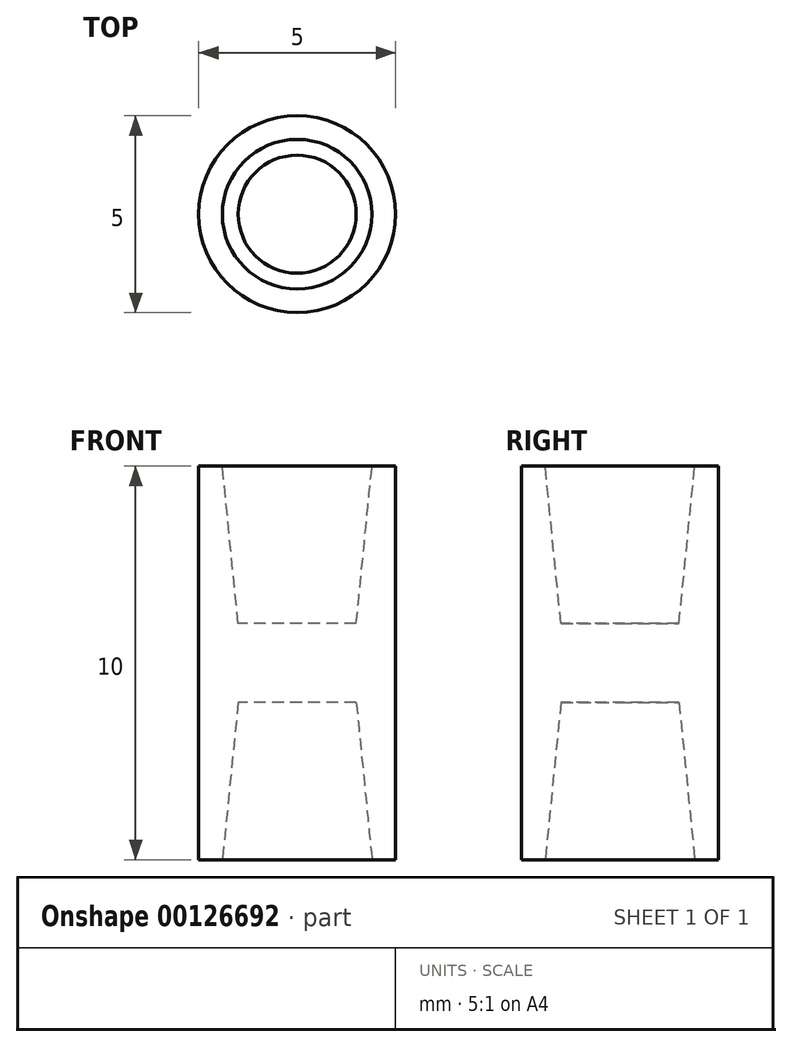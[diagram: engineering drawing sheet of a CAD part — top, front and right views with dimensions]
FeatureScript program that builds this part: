
annotation { "Feature Type Name" : "Feature", "Feature Type Description" : "" }
export const myFeature = defineFeature(function(context is Context, id is Id, definition is map)
    precondition{}
    {
        {
            var Q0;
            Q0=qCreatedBy(makeId("Top.planeOp"),FACE);
            var sketch = newSketch(context, id + "F0", { "sketchPlane" : qUnion([Q0])});
            skCircle(sketch, "E0", {"center": v(0, 0) * mm, "radius": 1.5 * mm});
            skCircle(sketch, "E1", {"center": v(0, 0) * mm, "radius": 2.5 * mm});
            skPoint(sketch, "E2", {"position": v(1.5, 0) * mm});
            skPoint(sketch, "E3", {"position": v(2.5, 0) * mm});
            skSolve(sketch);
        }
        {
            var Q0;
            Q0=makeQuery(id+"F0.imprint","IMPRINT",FACE,{"disambiguationData":[TD([[makeQuery(id+"F0.imprint","IMPRINT",EDGE,{"derivedFrom":sQuery(id+"F0.wireOp",EDGE,"E0")}),1.0]])]});
            extrude(context, id + "F1", {"entities" : qUnion([Q0]), "endBound" : BoundingType.SYMMETRIC, "depth" : 2 * mm});
        }
        {
            var Q0;
            Q0=makeQuery(id+"F0.imprint","IMPRINT",FACE,{"disambiguationData":[TD([[makeQuery(id+"F0.imprint","IMPRINT",EDGE,{"derivedFrom":sQuery(id+"F0.wireOp",EDGE,"E0")}),-1.0]])]});
            extrude(context, id + "F2", {"entities" : qUnion([Q0]), "operationType" : NewBodyOperationType.ADD, "endBound" : BoundingType.SYMMETRIC, "depth" : 10 * mm});
        }
        {
            var Q0;
            Q0=makeQuery(id+"F2.opExtrude","CAP_EDGE",EDGE,{"disambiguationData":[OSD([sQuery(id+"F0.wireOp",EDGE,"E0")])],"isStart":false});
            chamfer(context, id + "F3", {"entities" : qUnion([Q0]), "chamferType" : ChamferType.TWO_OFFSETS, "width1" : 4 * mm, "oppositeDirection" : false, "width2" : .4 * mm, "tangentPropagation" : true});
        }
        {
            var Q0;
            Q0=makeQuery(id+"F2.opExtrude","CAP_EDGE",EDGE,{"disambiguationData":[OSD([sQuery(id+"F0.wireOp",EDGE,"E0")])],"isStart":true});
            chamfer(context, id + "F4", {"entities" : qUnion([Q0]), "chamferType" : ChamferType.TWO_OFFSETS, "width1" : 0.4 * mm, "oppositeDirection" : false, "width2" : 4 * mm, "tangentPropagation" : true});
        }
    });
